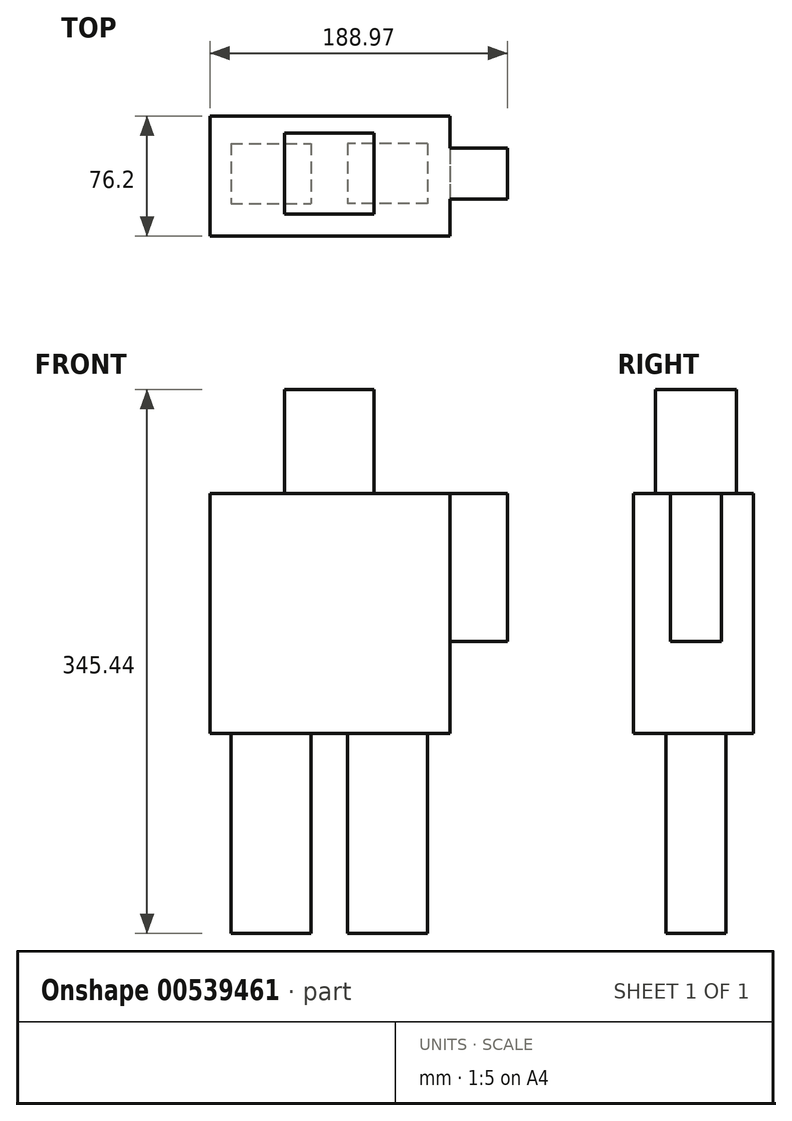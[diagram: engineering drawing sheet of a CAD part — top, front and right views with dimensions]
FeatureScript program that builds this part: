
annotation { "Feature Type Name" : "Feature", "Feature Type Description" : "" }
export const myFeature = defineFeature(function(context is Context, id is Id, definition is map)
    precondition{}
    {
        {
            var Q0;
            Q0=qCreatedBy(makeId("Top.planeOp"),FACE);
            var sketch = newSketch(context, id + "F0", { "sketchPlane" : qUnion([Q0])});
            skLineSegment(sketch, "E0.bottom", {"start": v(-62.48, 19.02) * mm, "end": v(-11.68, 19.02) * mm});
            skLineSegment(sketch, "E0.top", {"start": v(-62.48, -19.08) * mm, "end": v(-11.68, -19.08) * mm});
            skLineSegment(sketch, "E0.left", {"start": v(-62.48, 19.02) * mm, "end": v(-62.48, -19.08) * mm});
            skLineSegment(sketch, "E0.right", {"start": v(-11.68, 19.02) * mm, "end": v(-11.68, -19.08) * mm});
            skLineSegment(sketch, "E1.MirrorCS", {"start": v(62.48, 19.02) * mm, "end": v(11.68, 19.02) * mm});
            skLineSegment(sketch, "E2.MirrorCS", {"start": v(11.68, 19.02) * mm, "end": v(11.68, -19.08) * mm});
            skLineSegment(sketch, "E3.MirrorCS", {"start": v(62.48, -19.08) * mm, "end": v(11.68, -19.08) * mm});
            skLineSegment(sketch, "E4.MirrorCS", {"start": v(62.48, 19.02) * mm, "end": v(62.48, -19.08) * mm});
            skSolve(sketch);
        }
        {
            var Q0;
            Q0=makeQuery(id+"F0.imprint","IMPRINT",FACE,{"disambiguationData":[TD([[makeQuery(id+"F0.imprint","IMPRINT",EDGE,{"derivedFrom":sQuery(id+"F0.wireOp",EDGE,"E0.bottom")}),-1.0]])]});
            var Q1;
            Q1=makeQuery(id+"F0.imprint","IMPRINT",FACE,{"disambiguationData":[TD([[makeQuery(id+"F0.imprint","IMPRINT",EDGE,{"derivedFrom":sQuery(id+"F0.wireOp",EDGE,"E1.MirrorCS")}),1.0]])]});
            extrude(context, id + "F1", {"entities" : qUnion([Q0, Q1]), "depth" : 127 * mm, "offsetDistance" : 25.4 * mm});
        }
        {
            var Q0;
            Q0=makeQuery(id+"F1.opExtrude","CAP_FACE",FACE,{"disambiguationData":[OSD([sQuery(id+"F0.wireOp",EDGE,"E0.bottom"),sQuery(id+"F0.wireOp",EDGE,"E0.top"),sQuery(id+"F0.wireOp",EDGE,"E0.left"),sQuery(id+"F0.wireOp",EDGE,"E0.right")])],"isStart":false});
            var sketch = newSketch(context, id + "F2", { "sketchPlane" : qUnion([Q0])});
            skLineSegment(sketch, "E5.bottom", {"start": v(-75.8, 36.43) * mm, "end": v(76.6, 36.43) * mm});
            skLineSegment(sketch, "E5.top", {"start": v(-75.8, -39.77) * mm, "end": v(76.6, -39.77) * mm});
            skLineSegment(sketch, "E5.left", {"start": v(-75.8, 36.43) * mm, "end": v(-75.8, -39.77) * mm});
            skLineSegment(sketch, "E5.right", {"start": v(76.6, 36.43) * mm, "end": v(76.6, -39.77) * mm});
            skSolve(sketch);
        }
        {
            var Q0;
            Q0=makeQuery(id+"F2.imprint","IMPRINT",FACE,{"disambiguationData":[TD([[makeQuery(id+"F2.imprint","IMPRINT",EDGE,{"derivedFrom":makeQuery(id+"F1.opExtrude","CAP_EDGE",EDGE,{"disambiguationData":[OSD([sQuery(id+"F0.wireOp",EDGE,"E0.bottom")])],"isStart":false})}),-1.0]])]});
            var Q1;
            Q1=makeQuery(id+"F2.imprint","IMPRINT",FACE,{"disambiguationData":[TD([[makeQuery(id+"F2.imprint","IMPRINT",EDGE,{"derivedFrom":sQuery(id+"F2.wireOp",EDGE,"E5.bottom")}),-1.0]])]});
            extrude(context, id + "F3", {"entities" : qUnion([Q0, Q1]), "depth" : 152.4 * mm, "offsetDistance" : 25.4 * mm});
        }
        {
            var Q0;
            Q0=makeQuery(id+"F3.opExtrude","CAP_FACE",FACE,{"disambiguationData":[OSD([sQuery(id+"F2.wireOp",EDGE,"E5.bottom"),sQuery(id+"F2.wireOp",EDGE,"E5.top"),sQuery(id+"F2.wireOp",EDGE,"E5.left"),sQuery(id+"F2.wireOp",EDGE,"E5.right")])],"isStart":false});
            var sketch = newSketch(context, id + "F4", { "sketchPlane" : qUnion([Q0])});
            skLineSegment(sketch, "E6.bottom", {"start": v(28.37, -25.65) * mm, "end": v(-28.37, -25.65) * mm});
            skLineSegment(sketch, "E6.top", {"start": v(28.37, 25.65) * mm, "end": v(-28.37, 25.65) * mm});
            skLineSegment(sketch, "E6.left", {"start": v(28.37, -25.65) * mm, "end": v(28.37, 25.65) * mm});
            skLineSegment(sketch, "E6.right", {"start": v(-28.37, -25.65) * mm, "end": v(-28.37, 25.65) * mm});
            skPoint(sketch, "E6.middle", {"position": v(0, 0) * mm});
            skSolve(sketch);
        }
        {
            var Q0;
            Q0 = qSketchRegion(id + "F4", true);
            var Q1;
            Q1=makeQuery(id+"F4.imprint","IMPRINT",FACE,{"disambiguationData":[TD([[makeQuery(id+"F4.imprint","IMPRINT",EDGE,{"derivedFrom":sQuery(id+"F4.wireOp",EDGE,"E6.bottom")}),-1.0]])]});
            extrude(context, id + "F5", {"entities" : qUnion([Q0, Q1]), "operationType" : NewBodyOperationType.ADD, "depth" : 66.04 * mm, "offsetDistance" : 25.4 * mm});
        }
        {
            var Q0;
            Q0=makeQuery(id+"F3.opExtrude","SWEPT_FACE",FACE,{"disambiguationData":[OSD([sQuery(id+"F2.wireOp",EDGE,"E5.right")])]});
            var sketch = newSketch(context, id + "F6", { "sketchPlane" : qUnion([Q0])});
            skLineSegment(sketch, "E7.bottom", {"start": v(16.18, 185.6) * mm, "end": v(-16.18, 185.6) * mm});
            skLineSegment(sketch, "E7.top", {"start": v(16.18, 279.4) * mm, "end": v(-16.18, 279.4) * mm});
            skLineSegment(sketch, "E7.left", {"start": v(16.18, 185.6) * mm, "end": v(16.18, 279.4) * mm});
            skLineSegment(sketch, "E7.right", {"start": v(-16.18, 185.6) * mm, "end": v(-16.18, 279.4) * mm});
            skPoint(sketch, "E7.middle", {"position": v(0, 232.5) * mm});
            skSolve(sketch);
        }
        {
            var Q0;
            Q0 = qSketchRegion(id + "F6", true);
            extrude(context, id + "F7", {"entities" : qUnion([Q0]), "operationType" : NewBodyOperationType.ADD, "depth" : 36.58 * mm, "offsetDistance" : 25.4 * mm});
        }
    });
